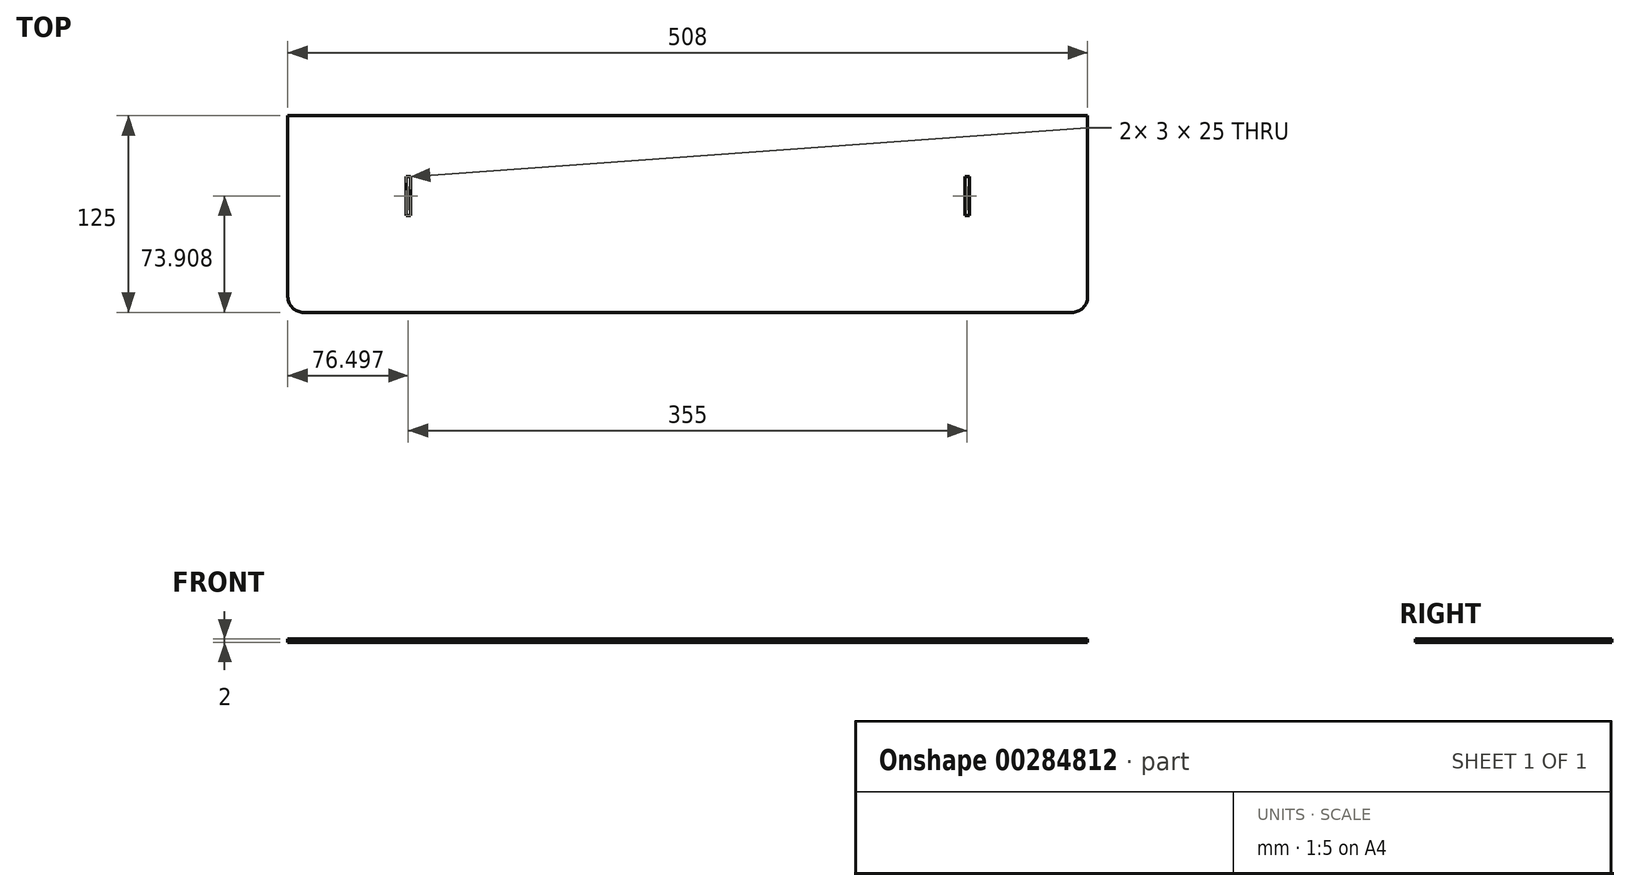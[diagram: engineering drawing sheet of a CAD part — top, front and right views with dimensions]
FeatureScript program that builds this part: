
annotation { "Feature Type Name" : "Feature", "Feature Type Description" : "" }
export const myFeature = defineFeature(function(context is Context, id is Id, definition is map)
    precondition{}
    {
        {
            var Q0;
            Q0=qCreatedBy(makeId("Top.planeOp"),FACE);
            var sketch = newSketch(context, id + "F0", { "sketchPlane" : qUnion([Q0])});
            skLineSegment(sketch, "E0.bottom", {"start": v(-272.36, 32.04) * mm, "end": v(235.64, 32.04) * mm});
            skLineSegment(sketch, "E0.top", {"start": v(-262.36, -92.96) * mm, "end": v(225.64, -92.96) * mm});
            skLineSegment(sketch, "E0.left", {"start": v(-272.36, 32.04) * mm, "end": v(-272.36, -82.96) * mm});
            skLineSegment(sketch, "E0.right", {"start": v(235.64, 32.04) * mm, "end": v(235.64, -82.96) * mm});
            skLineSegment(sketch, "E1.bottom", {"start": v(-197.36, -6.55) * mm, "end": v(-194.36, -6.55) * mm});
            skLineSegment(sketch, "E1.top", {"start": v(-197.36, -31.55) * mm, "end": v(-194.36, -31.55) * mm});
            skLineSegment(sketch, "E1.left", {"start": v(-197.36, -6.55) * mm, "end": v(-197.36, -31.55) * mm});
            skLineSegment(sketch, "E1.right", {"start": v(-194.36, -6.55) * mm, "end": v(-194.36, -31.55) * mm});
            skLineSegment(sketch, "E2.bottom", {"start": v(157.64, -6.55) * mm, "end": v(160.64, -6.55) * mm});
            skLineSegment(sketch, "E2.top", {"start": v(157.64, -31.55) * mm, "end": v(160.64, -31.55) * mm});
            skLineSegment(sketch, "E2.left", {"start": v(157.64, -6.55) * mm, "end": v(157.64, -31.55) * mm});
            skLineSegment(sketch, "E2.right", {"start": v(160.64, -6.55) * mm, "end": v(160.64, -31.55) * mm});
            skPoint(sketch, "E3.visualSharp", {"position": v(-272.36, -92.96) * mm});
            skArc(sketch, "E3.filletArc", {"start": v(-272.36, -82.96) * mm, "mid": v(-269.43, -90.03) * mm, "end": v(-262.36, -92.96) * mm});
            skPoint(sketch, "E4.visualSharp", {"position": v(235.64, -92.96) * mm});
            skArc(sketch, "E4.filletArc", {"start": v(225.64, -92.96) * mm, "mid": v(232.7, -90.03) * mm, "end": v(235.64, -82.96) * mm});
            skSolve(sketch);
        }
        {
            var Q0;
            Q0=makeQuery(id+"F0.imprint","IMPRINT",FACE,{"disambiguationData":[TD([[makeQuery(id+"F0.imprint","IMPRINT",EDGE,{"derivedFrom":sQuery(id+"F0.wireOp",EDGE,"E0.bottom")}),-1.0]])]});
            extrude(context, id + "F1", {"entities" : qUnion([Q0]), "depth" : 2 * mm, "offsetDistance" : 25 * mm});
        }
    });
